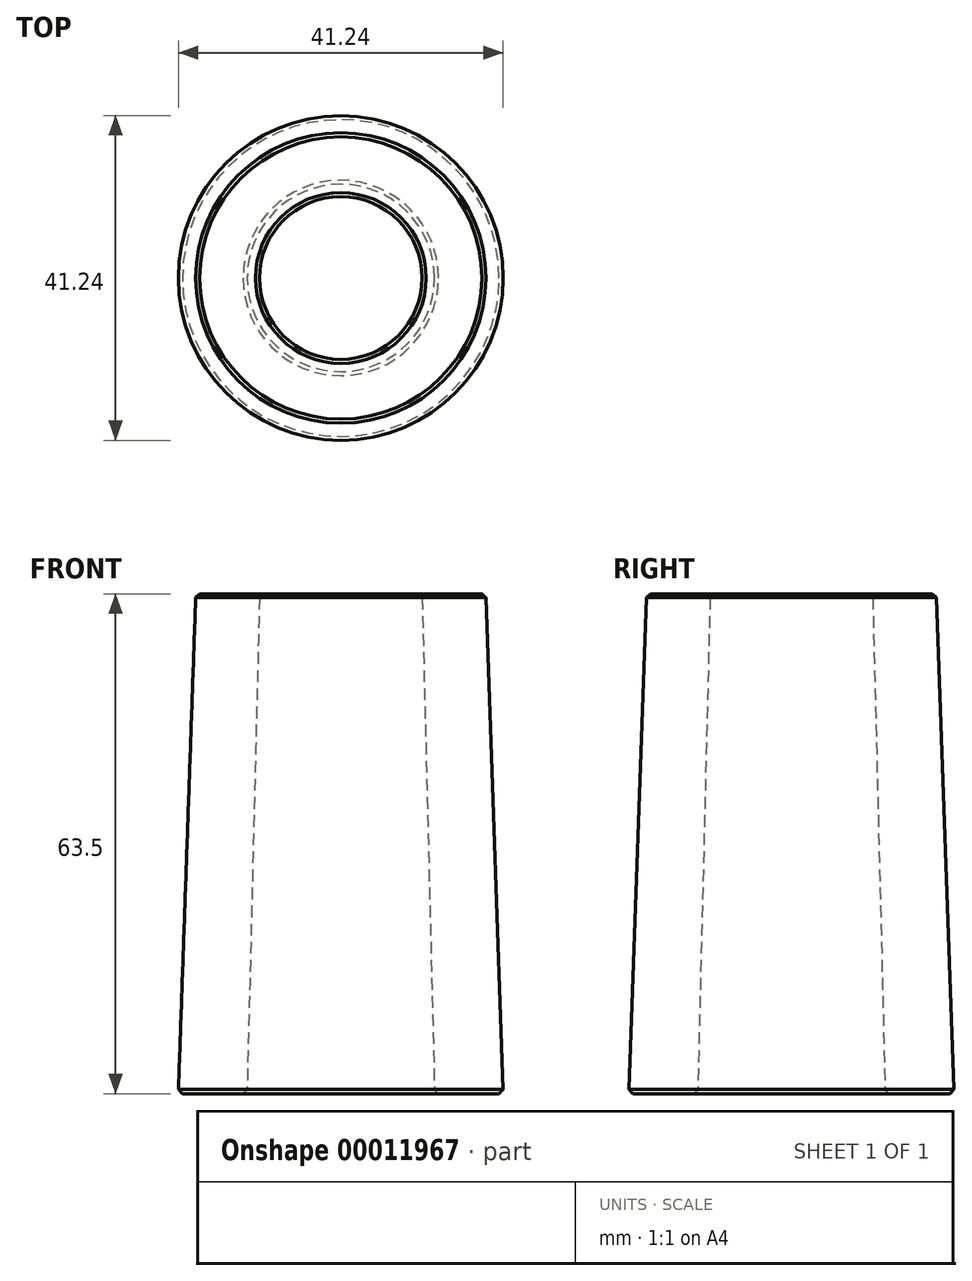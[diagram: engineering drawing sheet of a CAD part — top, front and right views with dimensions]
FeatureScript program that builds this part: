
annotation { "Feature Type Name" : "Feature", "Feature Type Description" : "" }
export const myFeature = defineFeature(function(context is Context, id is Id, definition is map)
    precondition{}
    {
        {
            var Q0;
            Q0=qCreatedBy(makeId("Front.planeOp"),FACE);
            var sketch = newSketch(context, id + "F0", { "sketchPlane" : qUnion([Q0])});
            skLineSegment(sketch, "E0", {"start": v(0, 63.5) * mm, "end": v(18.42, 63.5) * mm, "construction": true});
            skLineSegment(sketch, "E1", {"start": v(18.42, 63.5) * mm, "end": v(20.64, 0) * mm});
            skLineSegment(sketch, "E2", {"start": v(20.64, 0) * mm, "end": v(0, 0) * mm, "construction": true});
            skLineSegment(sketch, "E3", {"start": v(0, 63.5) * mm, "end": v(0, 0) * mm, "construction": true});
            skLineSegment(sketch, "E4", {"start": v(11.91, 0) * mm, "end": v(10.32, 63.5) * mm});
            skLineSegment(sketch, "E5", {"start": v(10.32, 63.5) * mm, "end": v(18.42, 63.5) * mm});
            skLineSegment(sketch, "E6", {"start": v(11.91, 0) * mm, "end": v(20.64, 0) * mm});
            skSolve(sketch);
        }
        {
            var Q0;
            Q0=makeQuery(id+"F0.imprint","IMPRINT",FACE,{"disambiguationData":[TD([[makeQuery(id+"F0.imprint","IMPRINT",EDGE,{"derivedFrom":sQuery(id+"F0.wireOp",EDGE,"E4")}),-1.0]])]});
            var Q1;
            Q1=sQuery(id+"F0.wireOp",EDGE,"E3");
            revolve(context, id + "F1", {"entities" : qUnion([Q0]), "axis" : qUnion([Q1]), "revolveType" : RevolveType.FULL});
        }
        {
            var Q0;
            Q0=makeQuery(id+"F1.opRevolve","SWEPT_EDGE",EDGE,{"disambiguationData":[OSD([sQuery(id+"F0.wireOp",EDGE,"E1"),sQuery(id+"F0.wireOp",EDGE,"E5")])]});
            var Q1;
            Q1=makeQuery(id+"F1.opRevolve","SWEPT_EDGE",EDGE,{"disambiguationData":[OSD([sQuery(id+"F0.wireOp",EDGE,"E4"),sQuery(id+"F0.wireOp",EDGE,"E5")])]});
            var Q2;
            Q2=makeQuery(id+"F1.opRevolve","SWEPT_EDGE",EDGE,{"disambiguationData":[OSD([sQuery(id+"F0.wireOp",EDGE,"E1"),sQuery(id+"F0.wireOp",EDGE,"E6")])]});
            var Q3;
            Q3=makeQuery(id+"F1.opRevolve","SWEPT_EDGE",EDGE,{"disambiguationData":[OSD([sQuery(id+"F0.wireOp",EDGE,"E4"),sQuery(id+"F0.wireOp",EDGE,"E6")])]});
            chamfer(context, id + "F2", {"entities" : qUnion([Q0, Q1, Q2, Q3]), "width" : 0.5 * mm, "tangentPropagation" : true});
        }
    });
